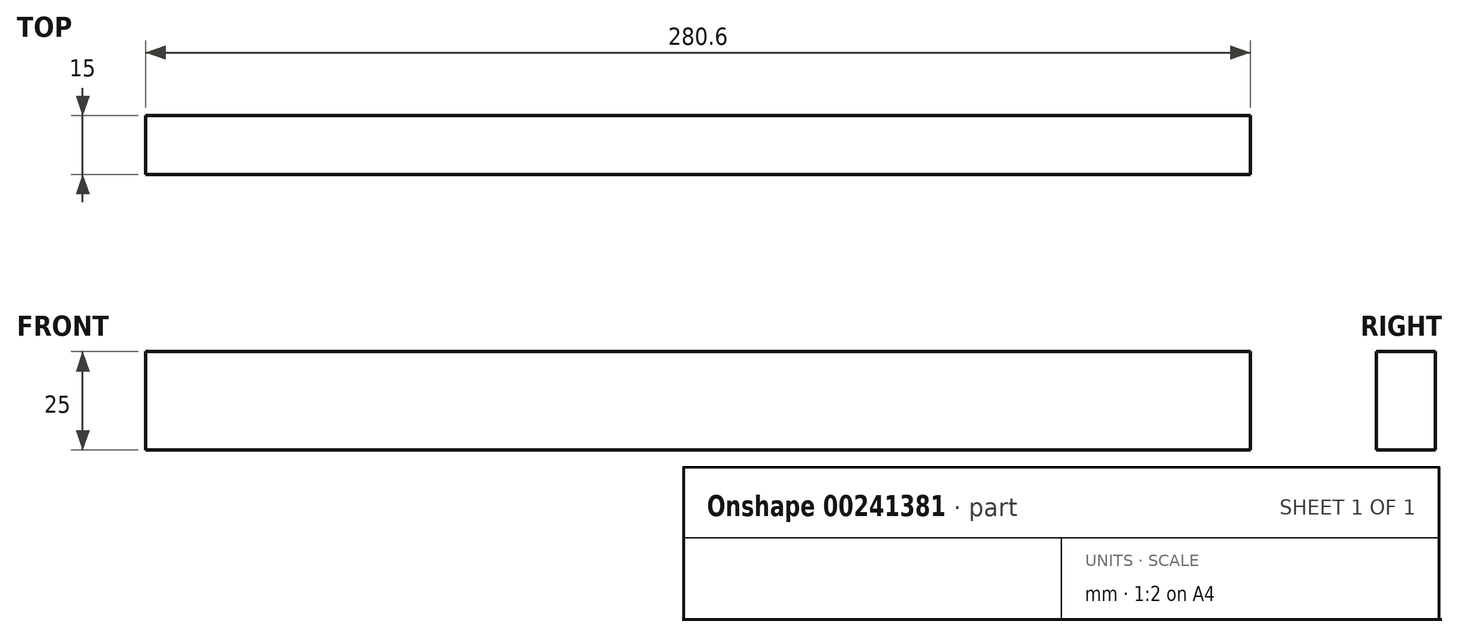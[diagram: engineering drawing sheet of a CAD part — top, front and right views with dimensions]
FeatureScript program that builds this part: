
annotation { "Feature Type Name" : "Feature", "Feature Type Description" : "" }
export const myFeature = defineFeature(function(context is Context, id is Id, definition is map)
    precondition{}
    {
        {
            var Q0;
            Q0=qCreatedBy(makeId("Right.planeOp"),FACE);
            var sketch = newSketch(context, id + "F0", { "sketchPlane" : qUnion([Q0])});
            skLineSegment(sketch, "E0.bottom", {"start": v(-7.5, 12.5) * mm, "end": v(7.5, 12.5) * mm});
            skLineSegment(sketch, "E0.top", {"start": v(-7.5, -12.5) * mm, "end": v(7.5, -12.5) * mm});
            skLineSegment(sketch, "E0.left", {"start": v(-7.5, 12.5) * mm, "end": v(-7.5, -12.5) * mm});
            skLineSegment(sketch, "E0.right", {"start": v(7.5, 12.5) * mm, "end": v(7.5, -12.5) * mm});
            skPoint(sketch, "E0.middle", {"position": v(0, 0) * mm});
            skSolve(sketch);
        }
        {
            var Q0;
            Q0 = qSketchRegion(id + "F0", true);
            extrude(context, id + "F1", {"entities" : qUnion([Q0]), "depth" : 280.6 * mm});
        }
    });
